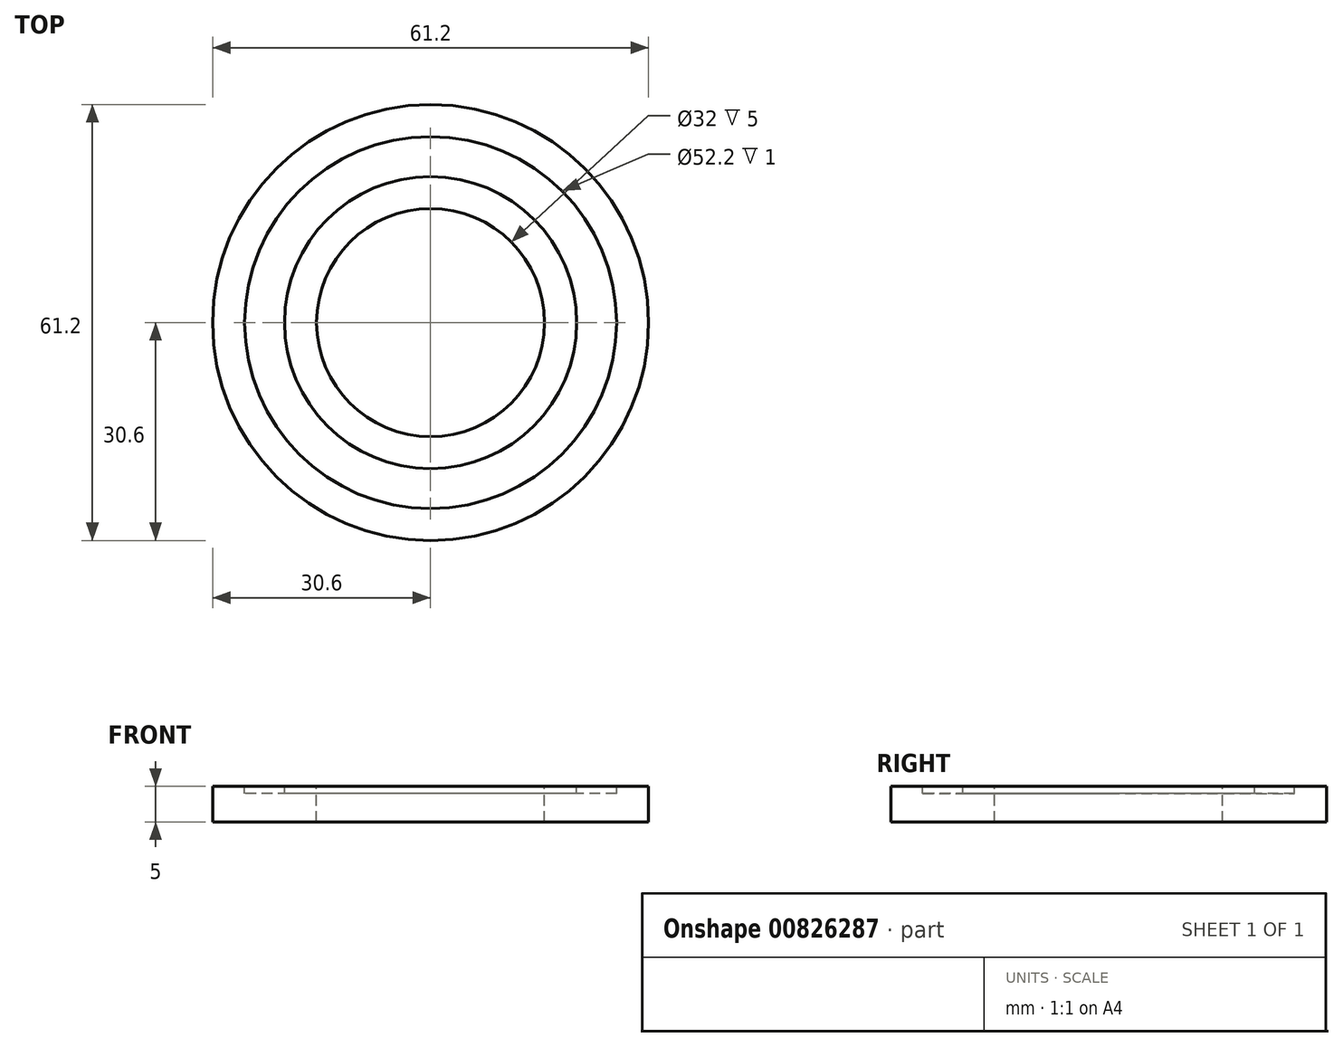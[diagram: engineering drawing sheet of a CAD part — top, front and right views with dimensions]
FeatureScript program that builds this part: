
annotation { "Feature Type Name" : "Feature", "Feature Type Description" : "" }
export const myFeature = defineFeature(function(context is Context, id is Id, definition is map)
    precondition{}
    {
        {
            var Q0;
            Q0=qCreatedBy(makeId("Top.planeOp"),FACE);
            var sketch = newSketch(context, id + "F0", { "sketchPlane" : qUnion([Q0])});
            skCircle(sketch, "E0", {"center": v(0, 0) * mm, "radius": 25.6 * mm});
            skCircle(sketch, "E1", {"center": v(0, 0) * mm, "radius": 21 * mm});
            skSolve(sketch);
        }
        {
            var Q0;
            Q0=qCreatedBy(makeId("Top.planeOp"),FACE);
            var sketch = newSketch(context, id + "F1", { "sketchPlane" : qUnion([Q0])});
            skCircle(sketch, "E2", {"center": v(0, 0) * mm, "radius": 30.6 * mm});
            skCircle(sketch, "E3", {"center": v(0, 0) * mm, "radius": 16 * mm});
            skSolve(sketch);
        }
        {
            var Q0;
            Q0 = qSketchRegion(id + "F1", true);
            extrude(context, id + "F2", {"entities" : qUnion([Q0]), "oppositeDirection" : true, "depth" : 5 * mm, "offsetDistance" : 25 * mm});
        }
        {
            var Q0;
            Q0=qCreatedBy(makeId("Top.planeOp"),FACE);
            var sketch = newSketch(context, id + "F3", { "sketchPlane" : qUnion([Q0])});
            skCircle(sketch, "E4", {"center": v(0, 0) * mm, "radius": 26.1 * mm});
            skCircle(sketch, "E5", {"center": v(0, 0) * mm, "radius": 20.5 * mm});
            skSolve(sketch);
        }
        {
            var Q0;
            Q0 = qSketchRegion(id + "F3", true);
            extrude(context, id + "F4", {"entities" : qUnion([Q0]), "operationType" : NewBodyOperationType.REMOVE, "oppositeDirection" : true, "depth" : 1 * mm, "offsetDistance" : 25 * mm});
        }
    });
